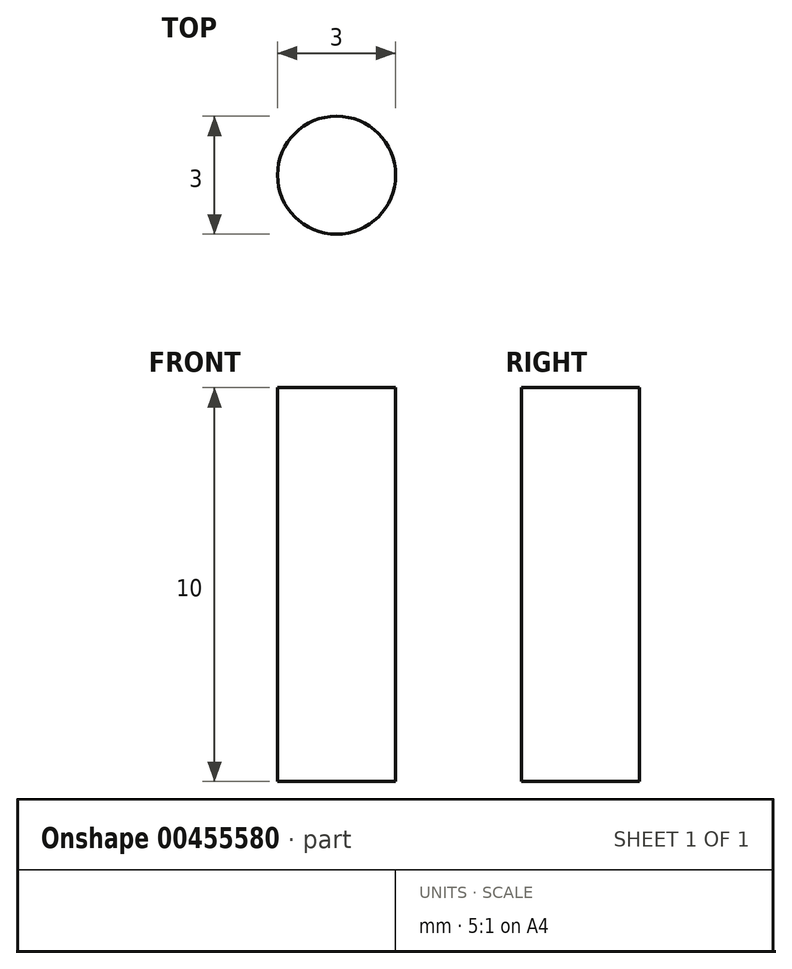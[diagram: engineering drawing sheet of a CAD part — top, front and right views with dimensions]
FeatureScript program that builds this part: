
annotation { "Feature Type Name" : "Feature", "Feature Type Description" : "" }
export const myFeature = defineFeature(function(context is Context, id is Id, definition is map)
    precondition{}
    {
        {
            var Q0;
            Q0=qCreatedBy(makeId("Top.planeOp"),FACE);
            var sketch = newSketch(context, id + "F0", { "sketchPlane" : qUnion([Q0])});
            skCircle(sketch, "E0", {"center": v(0, 137.95) * mm, "radius": 1.5 * mm});
            skCircle(sketch, "E1", {"center": v(-8, 129.95) * mm, "radius": 1.5 * mm});
            skCircle(sketch, "E2", {"center": v(58, 129.95) * mm, "radius": 10.5 * mm});
            skCircle(sketch, "E3", {"center": v(-104.5, -146.05) * mm, "radius": 1.55 * mm});
            skCircle(sketch, "E4", {"center": v(104.5, 62.95) * mm, "radius": 1.55 * mm});
            skLineSegment(sketch, "E5", {"start": v(-86.7, 145.05) * mm, "end": v(-86.7, 72.95) * mm});
            skLineSegment(sketch, "E6", {"start": v(86.7, 72.95) * mm, "end": v(86.7, 145.05) * mm});
            skLineSegment(sketch, "E7", {"start": v(81.7, 150.05) * mm, "end": v(-81.7, 150.05) * mm});
            skCircle(sketch, "E8", {"center": v(-104.5, 62.95) * mm, "radius": 1.55 * mm});
            skCircle(sketch, "E9", {"center": v(104.5, -146.05) * mm, "radius": 1.55 * mm});
            skCircle(sketch, "E10", {"center": v(-58, 129.95) * mm, "radius": 10.5 * mm});
            skCircle(sketch, "E11", {"center": v(0, 129.95) * mm, "radius": 5.1 * mm});
            skCircle(sketch, "E12", {"center": v(8, 129.95) * mm, "radius": 1.5 * mm});
            skCircle(sketch, "E13", {"center": v(0, 121.95) * mm, "radius": 1.5 * mm});
            skLineSegment(sketch, "E14.bottom", {"start": v(104.5, 62.95) * mm, "end": v(-104.5, 62.95) * mm, "construction": true});
            skLineSegment(sketch, "E14.top", {"start": v(104.5, -146.05) * mm, "end": v(-104.5, -146.05) * mm, "construction": true});
            skLineSegment(sketch, "E14.left", {"start": v(104.5, 62.95) * mm, "end": v(104.5, -146.05) * mm, "construction": true});
            skLineSegment(sketch, "E14.right", {"start": v(-104.5, 62.95) * mm, "end": v(-104.5, -146.05) * mm, "construction": true});
            skLineSegment(sketch, "E15.0", {"start": v(-109.5, 62.95) * mm, "end": v(-109.5, -146.05) * mm});
            skLineSegment(sketch, "E15.1", {"start": v(104.5, 67.95) * mm, "end": v(91.7, 67.95) * mm});
            skLineSegment(sketch, "E15.2", {"start": v(109.5, 62.95) * mm, "end": v(109.5, -146.05) * mm});
            skLineSegment(sketch, "E15.3", {"start": v(104.5, -151.05) * mm, "end": v(-104.5, -151.05) * mm});
            skLineSegment(sketch, "E16.trimOffspring", {"start": v(-91.7, 67.95) * mm, "end": v(-104.5, 67.95) * mm});
            skCircle(sketch, "E17", {"center": v(-58, 129.95) * mm, "radius": 16 * mm, "construction": true});
            skCircle(sketch, "E18", {"center": v(58, 129.95) * mm, "radius": 16 * mm, "construction": true});
            skCircle(sketch, "E19", {"center": v(-69.31, 141.26) * mm, "radius": 2 * mm});
            skCircle(sketch, "E20.1.0", {"center": v(-46.69, 141.26) * mm, "radius": 2 * mm});
            skCircle(sketch, "E20.2.0", {"center": v(-46.69, 118.64) * mm, "radius": 2 * mm});
            skCircle(sketch, "E20.3.0", {"center": v(-69.31, 118.64) * mm, "radius": 2 * mm});
            skCircle(sketch, "E21", {"center": v(46.69, 141.26) * mm, "radius": 2 * mm});
            skCircle(sketch, "E22.1.0", {"center": v(69.31, 141.26) * mm, "radius": 2 * mm});
            skCircle(sketch, "E22.2.0", {"center": v(69.31, 118.64) * mm, "radius": 2 * mm});
            skCircle(sketch, "E22.3.0", {"center": v(46.69, 118.64) * mm, "radius": 2 * mm});
            skPoint(sketch, "E23.visualSharp", {"position": v(-109.5, 67.95) * mm});
            skArc(sketch, "E23.filletArc", {"start": v(-104.5, 67.95) * mm, "mid": v(-108.04, 66.49) * mm, "end": v(-109.5, 62.95) * mm});
            skPoint(sketch, "E24.visualSharp", {"position": v(109.5, 67.95) * mm});
            skArc(sketch, "E24.filletArc", {"start": v(109.5, 62.95) * mm, "mid": v(108.04, 66.49) * mm, "end": v(104.5, 67.95) * mm});
            skPoint(sketch, "E25.visualSharp", {"position": v(109.5, -151.05) * mm});
            skArc(sketch, "E25.filletArc", {"start": v(104.5, -151.05) * mm, "mid": v(108.04, -149.59) * mm, "end": v(109.5, -146.05) * mm});
            skPoint(sketch, "E26.visualSharp", {"position": v(-109.5, -151.05) * mm});
            skArc(sketch, "E26.filletArc", {"start": v(-109.5, -146.05) * mm, "mid": v(-108.04, -149.59) * mm, "end": v(-104.5, -151.05) * mm});
            skPoint(sketch, "E27.visualSharp", {"position": v(-86.7, 150.05) * mm});
            skArc(sketch, "E27.filletArc", {"start": v(-81.7, 150.05) * mm, "mid": v(-85.24, 148.59) * mm, "end": v(-86.7, 145.05) * mm});
            skPoint(sketch, "E28.visualSharp", {"position": v(86.7, 150.05) * mm});
            skArc(sketch, "E28.filletArc", {"start": v(86.7, 145.05) * mm, "mid": v(85.24, 148.59) * mm, "end": v(81.7, 150.05) * mm});
            skPoint(sketch, "E29.visualSharp", {"position": v(86.7, 67.95) * mm});
            skArc(sketch, "E29.filletArc", {"start": v(86.7, 72.95) * mm, "mid": v(88.16, 69.41) * mm, "end": v(91.7, 67.95) * mm});
            skPoint(sketch, "E30.visualSharp", {"position": v(-86.7, 67.95) * mm});
            skArc(sketch, "E30.filletArc", {"start": v(-91.7, 67.95) * mm, "mid": v(-88.16, 69.41) * mm, "end": v(-86.7, 72.95) * mm});
            skLineSegment(sketch, "E31", {"start": v(104.5, 62.95) * mm, "end": v(-104.5, -146.05) * mm, "construction": true});
            skLineSegment(sketch, "E32", {"start": v(-104.5, 62.95) * mm, "end": v(104.5, -146.05) * mm, "construction": true});
            skLineSegment(sketch, "E33", {"start": v(0, -151.05) * mm, "end": v(0, 150.05) * mm, "construction": true});
            skLineSegment(sketch, "E34", {"start": v(-109.5, -41.55) * mm, "end": v(109.5, -41.55) * mm, "construction": true});
            skCircle(sketch, "E35", {"center": v(0, 62.95) * mm, "radius": 1.55 * mm});
            skLineSegment(sketch, "E36", {"start": v(-84, 54.95) * mm, "end": v(-8, -21.06) * mm});
            skLineSegment(sketch, "E37", {"start": v(-8, -21.06) * mm, "end": v(-8, 54.95) * mm});
            skLineSegment(sketch, "E38", {"start": v(-8, 54.95) * mm, "end": v(-84, 54.95) * mm});
            skLineSegment(sketch, "E39.MirrorCS", {"start": v(-96.5, 42.46) * mm, "end": v(-20.5, -33.55) * mm});
            skLineSegment(sketch, "E40.MirrorCS", {"start": v(-96.5, -33.55) * mm, "end": v(-96.5, 42.46) * mm});
            skLineSegment(sketch, "E41.MirrorCS", {"start": v(-20.5, -33.55) * mm, "end": v(-96.5, -33.55) * mm});
            skLineSegment(sketch, "E42.MirrorCS", {"start": v(8, -21.06) * mm, "end": v(8, 54.95) * mm});
            skLineSegment(sketch, "E43.MirrorCS", {"start": v(8, 54.95) * mm, "end": v(84, 54.95) * mm});
            skLineSegment(sketch, "E44.MirrorCS", {"start": v(84, 54.95) * mm, "end": v(8, -21.06) * mm});
            skLineSegment(sketch, "E45.MirrorCS", {"start": v(84, -138.05) * mm, "end": v(8, -62.04) * mm});
            skLineSegment(sketch, "E46.MirrorCS", {"start": v(8, -138.05) * mm, "end": v(84, -138.05) * mm});
            skLineSegment(sketch, "E47.MirrorCS", {"start": v(8, -62.04) * mm, "end": v(8, -138.05) * mm});
            skLineSegment(sketch, "E48.MirrorCS", {"start": v(-8, -62.04) * mm, "end": v(-8, -138.05) * mm});
            skLineSegment(sketch, "E49.MirrorCS", {"start": v(-8, -138.05) * mm, "end": v(-84, -138.05) * mm});
            skLineSegment(sketch, "E50.MirrorCS", {"start": v(-84, -138.05) * mm, "end": v(-8, -62.04) * mm});
            skLineSegment(sketch, "E51.MirrorCS", {"start": v(-96.5, -49.55) * mm, "end": v(-96.5, -125.56) * mm});
            skLineSegment(sketch, "E52.MirrorCS", {"start": v(-96.5, -125.56) * mm, "end": v(-20.5, -49.55) * mm});
            skLineSegment(sketch, "E53.MirrorCS", {"start": v(-20.5, -49.55) * mm, "end": v(-96.5, -49.55) * mm});
            skLineSegment(sketch, "E54.MirrorCS", {"start": v(96.5, -125.56) * mm, "end": v(20.5, -49.55) * mm});
            skLineSegment(sketch, "E55.MirrorCS", {"start": v(96.5, -49.55) * mm, "end": v(96.5, -125.56) * mm});
            skLineSegment(sketch, "E56.MirrorCS", {"start": v(20.5, -49.55) * mm, "end": v(96.5, -49.55) * mm});
            skLineSegment(sketch, "E57.MirrorCS", {"start": v(20.5, -33.55) * mm, "end": v(96.5, -33.55) * mm});
            skLineSegment(sketch, "E58.MirrorCS", {"start": v(96.5, 42.46) * mm, "end": v(20.5, -33.55) * mm});
            skLineSegment(sketch, "E59.MirrorCS", {"start": v(96.5, -33.55) * mm, "end": v(96.5, 42.46) * mm});
            skSolve(sketch);
        }
        {
            var Q0;
            Q0=makeQuery(id+"F0.imprint","IMPRINT",FACE,{"disambiguationData":[TD([[makeQuery(id+"F0.imprint","IMPRINT",EDGE,{"derivedFrom":sQuery(id+"F0.wireOp",EDGE,"E0")}),1.0]])]});
            extrude(context, id + "F1", {"entities" : qUnion([Q0]), "depth" : 10 * mm});
        }
    });
